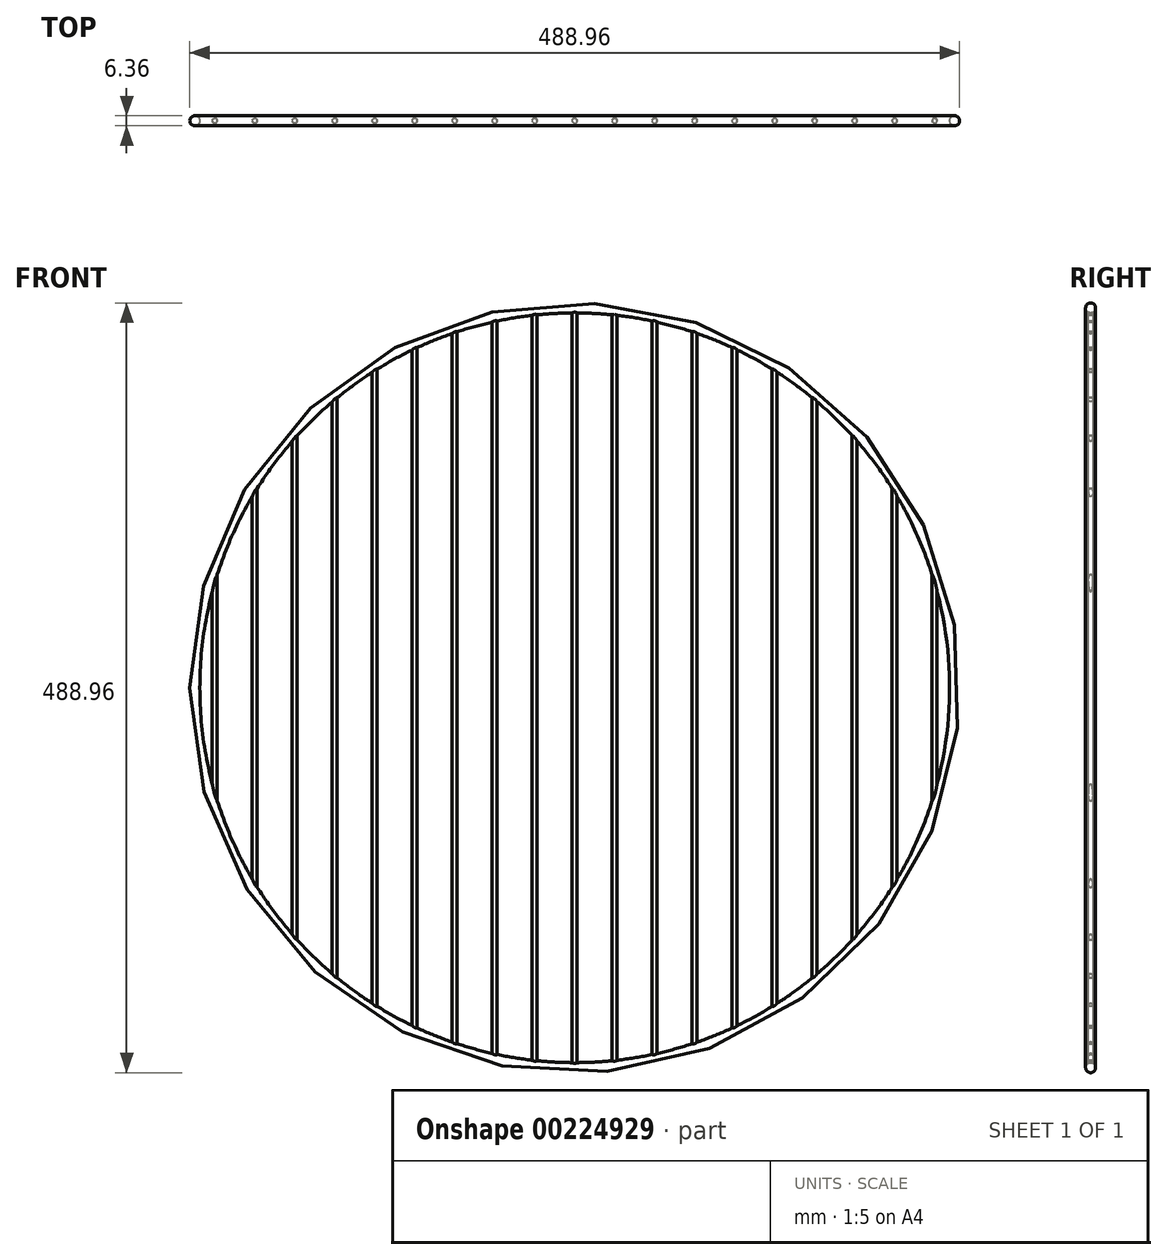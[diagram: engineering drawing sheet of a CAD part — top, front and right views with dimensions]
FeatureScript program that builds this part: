
annotation { "Feature Type Name" : "Feature", "Feature Type Description" : "" }
export const myFeature = defineFeature(function(context is Context, id is Id, definition is map)
    precondition{}
    {
        {
            var Q0;
            Q0=qCreatedBy(makeId("Top.planeOp"),FACE);
            var sketch = newSketch(context, id + "F0", { "sketchPlane" : qUnion([Q0])});
            skLineSegment(sketch, "E0", {"start": v(0, 13.36) * mm, "end": v(0, -17.67) * mm, "construction": true});
            skCircle(sketch, "E1", {"center": v(241.3, 0) * mm, "radius": 3.18 * mm});
            skSolve(sketch);
        }
        {
            var Q0;
            Q0 = qSketchRegion(id + "F0", true);
            var Q1;
            Q1=sQuery(id+"F0.wireOp",EDGE,"E0");
            revolve(context, id + "F1", {"entities" : qUnion([Q0]), "axis" : qUnion([Q1]), "revolveType" : RevolveType.FULL});
        }
        {
            var Q0;
            Q0=qCreatedBy(makeId("Top.planeOp"),FACE);
            var sketch = newSketch(context, id + "F2", { "sketchPlane" : qUnion([Q0])});
            skCircle(sketch, "E2", {"center": v(0, 0) * mm, "radius": 1.59 * mm});
            skCircle(sketch, "E3.1.0.0", {"center": v(25.4, 0) * mm, "radius": 1.59 * mm});
            skCircle(sketch, "E3.2.0.0", {"center": v(50.8, 0) * mm, "radius": 1.59 * mm});
            skCircle(sketch, "E3.3.0.0", {"center": v(76.2, 0) * mm, "radius": 1.59 * mm});
            skCircle(sketch, "E3.4.0.0", {"center": v(101.6, 0) * mm, "radius": 1.59 * mm});
            skCircle(sketch, "E3.5.0.0", {"center": v(127, 0) * mm, "radius": 1.59 * mm});
            skCircle(sketch, "E3.6.0.0", {"center": v(152.4, 0) * mm, "radius": 1.59 * mm});
            skCircle(sketch, "E3.7.0.0", {"center": v(177.8, 0) * mm, "radius": 1.59 * mm});
            skCircle(sketch, "E3.8.0.0", {"center": v(203.2, 0) * mm, "radius": 1.59 * mm});
            skCircle(sketch, "E3.9.0.0", {"center": v(228.6, 0) * mm, "radius": 1.59 * mm});
            skLineSegment(sketch, "E3.direction1", {"start": v(0, 0) * mm, "end": v(25.4, 0) * mm, "construction": true});
            skCircle(sketch, "E4.1.0.0", {"center": v(-25.4, 0) * mm, "radius": 1.59 * mm});
            skCircle(sketch, "E4.2.0.0", {"center": v(-50.8, 0) * mm, "radius": 1.59 * mm});
            skCircle(sketch, "E4.3.0.0", {"center": v(-76.2, 0) * mm, "radius": 1.59 * mm});
            skCircle(sketch, "E4.4.0.0", {"center": v(-101.6, 0) * mm, "radius": 1.59 * mm});
            skCircle(sketch, "E4.5.0.0", {"center": v(-127, 0) * mm, "radius": 1.59 * mm});
            skCircle(sketch, "E4.6.0.0", {"center": v(-152.4, 0) * mm, "radius": 1.59 * mm});
            skCircle(sketch, "E4.7.0.0", {"center": v(-177.8, 0) * mm, "radius": 1.59 * mm});
            skCircle(sketch, "E4.8.0.0", {"center": v(-203.2, 0) * mm, "radius": 1.59 * mm});
            skCircle(sketch, "E4.9.0.0", {"center": v(-228.6, 0) * mm, "radius": 1.59 * mm});
            skLineSegment(sketch, "E4.direction1", {"start": v(0, 0) * mm, "end": v(-25.4, 0) * mm, "construction": true});
            skSolve(sketch);
        }
        {
            var Q0;
            Q0 = qSketchRegion(id + "F2", true);
            extrude(context, id + "F3", {"entities" : qUnion([Q0]), "operationType" : NewBodyOperationType.ADD, "endBound" : BoundingType.UP_TO_NEXT, "depth" : 25.4 * mm, "hasSecondDirection" : true, "secondDirectionBound" : BoundingType.UP_TO_NEXT, "secondDirectionOppositeDirection" : true, "secondDirectionDepth" : 25.4 * mm});
        }
    });
